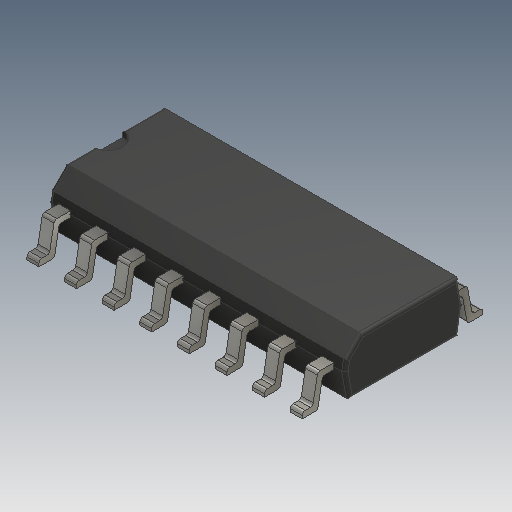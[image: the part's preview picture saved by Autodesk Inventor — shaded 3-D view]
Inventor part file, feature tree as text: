
AUTODESK INVENTOR PART (.ipt)
format: ipt  version: 2018 (Build 220112000, 112)  size: 460,288 bytes
history: native  units: mm
features: other x7, sketch x6, extrude x5, projected_geometry x3, fillet x2, chamfer x1, plane x1, pattern_linear x1, mirror x1
ambient origin geometry x8: Origin, YZ Plane, XZ Plane, XY Plane, X Axis, Y Axis, Z Axis, Center Point
bodies: Solid1 (feature_tree)
feature tree (27):
  other  "Table"
  other  "soic-8-N"
  other  "soic-8-W"
  other  "soic-14-N"
  other  "soic-14-W"
  other  "soic-16-N"
  other  "soic-16-W"
  extrude  "Extrusion1"  Depth=10.0mm
  chamfer  "Chamfer1"  Distance=2.0mm Angle=45.0deg
  extrude  "Extrusion2"  Depth=0.2mm
  plane  "Work Plane1"
  extrude  "Extrusion3"  Depth=0.1075mm
  fillet  "Fillet1"  Radius=0.15mm
  pattern_linear  "Rectangular Pattern1"  Spacing1=1.745329mm  [1 undecoded]
  mirror  "Mirror1"
  extrude  "Extrusion4"  Depth=0.1075mm
  extrude  "Extrusion5"  Depth=0.1075mm
  fillet  "Fillet2"  [1 undecoded]
  sketch  "Sketch3"  dims[d3=0.0mm]
  sketch  "Sketch1"  dims[d0=4.0mm d1=10.0mm]
  sketch  "Sketch2"  dims[d2=1.72mm]
  projected_geometry  "Projected Loop1"
  sketch  "Sketch4"  dims[d4=0.573333mm d5=2.0mm d6=45.0deg]
  sketch  "Sketch5"  dims[d7=-0.3175mm d8=0.2mm]
  projected_geometry  "Projected Loop2"
  sketch  "Sketch6"  dims[d13=0.2mm d15=0.2mm d16=0.15mm d18=1.745329mm d19=1.745329mm d21=1.72mm d22=0.0mm d23=0.525mm d24=0.525mm d25=0.1mm d26=0.4mm d27=0.0mm d28=0.1mm d29=78.740157mm d31=1.27mm d32=0.4mm d33=0.0mm d34=1.0mm d35=0.215mm d36=0.0mm d37=0.1075mm d38=2.0mm]
  projected_geometry  "Projected Loop3"
note: 2 required parameter values undecoded (feature->parameter linkage not recoverable at this tier; creation-order binding heuristic only, values carry confidence <= 0.55)
